# Revit family: Lockers_Cell_Phone-With_Access_Panel-Salsbury_Industries-Surface_Mounted-3_Door_High_Units-8_Inch_Deep
name_source: partatom
category: Specialty Equipment
revit_build: Autodesk Revit 2016 (Build: 20150714_1515(x64)
units: mm (PartAtom-declared; Revit-internal decimal feet)

## family parameters
Cut with Voids When Loaded = No
Host = Face
OmniClass Number = 23.40.00.00
OmniClass Title = Equipment and Furnishings
Part Type = Normal
Room Calculation Point = No
Round Connector Dimension = Use Diameter
Shared = No

## types (8) — shared parameters
Assembly Code = C1030310
Assembly Description = Lockers
Back Enclosure Material = Aluminum - Salsbury Finish - Clear
Back of Doors - Alignment = 8.917 "
Column Divider 1 = Yes
Column Divider 2 = Yes
Column Divider 3 = Yes
Compartment Depth = 8.293 "
Depth = 9.25 "
Dial Numbering = Paint - Salsbury Finish - White
Door Slot L2 = A and B Access Doors : A Door - Access
Door Window Material = Plastic - Salsbury Finish - Clear
Lock Material = Stainless Steel - Salsbury Finish -  Polished
Manufacturer = Salsbury Industries
MasterFormat Number = 10 51 00
MasterFormat Title = Lockers
OmniClass 23 Number = 23.40.00.00
OmniClass 23 Title = Equipment and Furnishings
Resettable Combination Lock = Plastic - Salsbury Finish - Black
Row Divider 4 = Yes
Row Divider 5 = Yes
Row Divider 6 = Yes
Row Divider 7 = Yes
Trim Height = 18.75 "
Type Comments = Cell Phone Lockers with Front Access Panel - Suface Mounted Unit
URL = www.lockers.com
Version = 2.0 (07/31/18)
Visible Door Number = Yes

## per-type parameters (varying)
| type | Column Divider 4 | Column Divider 5 | Description | Door Slot L1 | Door Slot L10 | Door Slot L11 | Door Slot L12 | Door Slot L13 | Door Slot L14 | Door Slot L15 | Door Slot L3 | Door Slot L4 | Door Slot L5 | Door Slot L6 | Door Slot L7 | Door Slot L8 | Door Slot L9 | Model | Width |
| 19138-15 with Keyed Locks | Yes | Yes | 15 A-Doors (14 Usable) with Keyed Locks - 3 Door High Unit | A and B Keyed Doors : A Door | A and B Keyed Doors : A Door | A and B Keyed Doors : A Door | A and B Keyed Doors : A Door | A and B Keyed Doors : A Door | A and B Keyed Doors : A Door | A and B Keyed Doors : A Door | A and B Keyed Doors : A Door | A and B Keyed Doors : A Door | A and B Keyed Doors : A Door | A and B Keyed Doors : A Door | A and B Keyed Doors : A Door | A and B Keyed Doors : A Door | A and B Keyed Doors : A Door | 19138-15 | 37 " |
| 19138-10 with Keyed Locks | Yes | No | 8 A-Doors (7 Usable) and 2 B-Doors with Keyed Locks - 3 Door High Unit | A and B Keyed Doors : A Door | A and B Keyed Doors : A Door | A and B Keyed Doors : A Door | A and B Keyed Doors : B Door | A and B Keyed Doors : None | A and B Keyed Doors : None | A and B Keyed Doors : None | A and B Keyed Doors : None | A and B Keyed Doors : A Door | A and B Keyed Doors : A Door | A and B Keyed Doors : B Door | A and B Keyed Doors : A Door | A and B Keyed Doors : A Door | A and B Keyed Doors : None | 19138-10 | 30.5 " |
| 19138-09 with Keyed Locks | No | No | 9 A-Doors (8 Usable) with Keyed Locks - 3 Door High Unit | A and B Keyed Doors : A Door | A and B Keyed Doors : None | A and B Keyed Doors : None | A and B Keyed Doors : None | A and B Keyed Doors : None | A and B Keyed Doors : None | A and B Keyed Doors : None | A and B Keyed Doors : A Door | A and B Keyed Doors : A Door | A and B Keyed Doors : A Door | A and B Keyed Doors : A Door | A and B Keyed Doors : A Door | A and B Keyed Doors : A Door | A and B Keyed Doors : A Door | 19138-09 | 24 " |
| 19138-15 with Resettable Combination Locks | Yes | Yes | 15 A-Doors (14 Usable) with Resettable Combination Locks - 3 Door High Unit | A and B Combination Doors : A Door- Combination Lock | A and B Combination Doors : A Door- Combination Lock | A and B Combination Doors : A Door- Combination Lock | A and B Combination Doors : A Door- Combination Lock | A and B Combination Doors : A Door- Combination Lock | A and B Combination Doors : A Door- Combination Lock | A and B Combination Doors : A Door- Combination Lock | A and B Combination Doors : A Door- Combination Lock | A and B Combination Doors : A Door- Combination Lock | A and B Combination Doors : A Door- Combination Lock | A and B Combination Doors : A Door- Combination Lock | A and B Combination Doors : A Door- Combination Lock | A and B Combination Doors : A Door- Combination Lock | A and B Combination Doors : A Door- Combination Lock | 19138-15 | 37 " |
| 19138-10 with Resettable Combination Locks | Yes | No | 8 A-Doors (7 Usable) and 2 B-Doors with Resettable Combination Locks - 3 Door High Unit | A and B Combination Doors : A Door- Combination Lock | A and B Combination Doors : A Door- Combination Lock | A and B Combination Doors : A Door- Combination Lock | A and B Combination Doors : B Door - Combination Lock | A and B Keyed Doors : None | A and B Keyed Doors : None | A and B Keyed Doors : None | A and B Keyed Doors : None | A and B Combination Doors : A Door- Combination Lock | A and B Combination Doors : A Door- Combination Lock | A and B Combination Doors : B Door - Combination Lock | A and B Combination Doors : A Door- Combination Lock | A and B Combination Doors : A Door- Combination Lock | A and B Keyed Doors : None | 19138-10 | 30.5 " |
| 19138-09 with Resettable Combination Locks | No | No | 9 A-Doors (8 Usable) with Resettable Combination Locks - 3 Door High Unit | A and B Combination Doors : A Door- Combination Lock | A and B Keyed Doors : None | A and B Keyed Doors : None | A and B Keyed Doors : None | A and B Keyed Doors : None | A and B Keyed Doors : None | A and B Keyed Doors : None | A and B Combination Doors : A Door- Combination Lock | A and B Combination Doors : A Door- Combination Lock | A and B Combination Doors : A Door- Combination Lock | A and B Combination Doors : A Door- Combination Lock | A and B Combination Doors : A Door- Combination Lock | A and B Combination Doors : A Door- Combination Lock | A and B Combination Doors : A Door- Combination Lock | 19138-09 | 24 " |
| 19138-06 with Keyed Locks | No | No | 6 A-Doors (5 Usable) with Keyed Locks - 3 Door High Unit | A and B Keyed Doors : A Door | A and B Keyed Doors : None | A and B Keyed Doors : None | A and B Keyed Doors : None | A and B Keyed Doors : None | A and B Keyed Doors : None | A and B Keyed Doors : None | A and B Keyed Doors : A Door | A and B Keyed Doors : A Door | A and B Keyed Doors : A Door | A and B Keyed Doors : A Door | A and B Keyed Doors : None | A and B Keyed Doors : None | A and B Keyed Doors : None | 19138-06 | 17.5 " |
| 19138-06 with Resettable Combination Locks | No | No | 6 A-Doors (5 Usable) with Resettable Combination Locks - 3 Door High Unit | A and B Combination Doors : A Door- Combination Lock | A and B Keyed Doors : None | A and B Keyed Doors : None | A and B Keyed Doors : None | A and B Keyed Doors : None | A and B Keyed Doors : None | A and B Keyed Doors : None | A and B Combination Doors : A Door- Combination Lock | A and B Combination Doors : A Door- Combination Lock | A and B Combination Doors : A Door- Combination Lock | A and B Combination Doors : A Door- Combination Lock | A and B Keyed Doors : None | A and B Keyed Doors : None | A and B Keyed Doors : None | 19138-06 | 17.5 " |

## geometry (parser evidence)
native form markers: Sweep x14
no freeform markers — native parametric forms only
